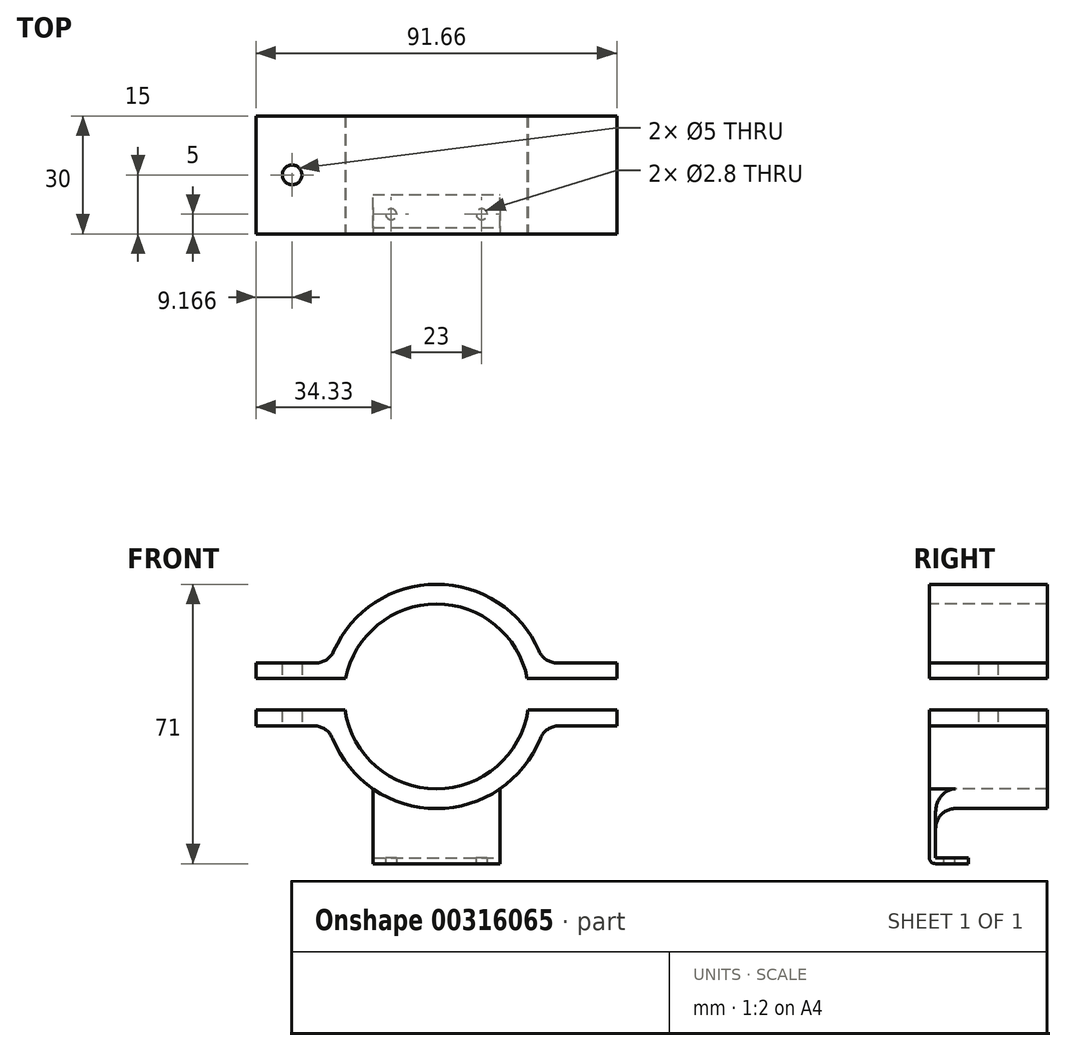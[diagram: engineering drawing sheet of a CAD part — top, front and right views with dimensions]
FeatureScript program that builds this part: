
annotation { "Feature Type Name" : "Feature", "Feature Type Description" : "" }
export const myFeature = defineFeature(function(context is Context, id is Id, definition is map)
    precondition{}
    {
        {
            var Q0;
            Q0=qCreatedBy(makeId("Top.planeOp"),FACE);
            var sketch = newSketch(context, id + "F0", { "sketchPlane" : qUnion([Q0])});
            skCircle(sketch, "E0", {"center": v(-11.5, 0) * mm, "radius": 1.4 * mm});
            skCircle(sketch, "E1", {"center": v(11.5, 0) * mm, "radius": 1.4 * mm});
            skLineSegment(sketch, "E2", {"start": v(-11.5, 0) * mm, "end": v(11.5, 0) * mm, "construction": true});
            skPoint(sketch, "E3", {"position": v(0, 0) * mm});
            skLineSegment(sketch, "E4.bottom", {"start": v(-16.14, -4.96) * mm, "end": v(16.14, -4.96) * mm});
            skLineSegment(sketch, "E4.top", {"start": v(-16.14, 4.96) * mm, "end": v(16.14, 4.96) * mm});
            skLineSegment(sketch, "E4.left", {"start": v(-16.14, -4.96) * mm, "end": v(-16.14, 4.96) * mm});
            skLineSegment(sketch, "E4.right", {"start": v(16.14, -4.96) * mm, "end": v(16.14, 4.96) * mm});
            skLineSegment(sketch, "E5", {"start": v(-11.5, 0) * mm, "end": v(-16.14, 0) * mm, "construction": true});
            skLineSegment(sketch, "E6", {"start": v(11.5, 0) * mm, "end": v(16.14, 0) * mm, "construction": true});
            skLineSegment(sketch, "E7", {"start": v(-11.5, 0) * mm, "end": v(-11.5, -4.96) * mm, "construction": true});
            skLineSegment(sketch, "E8", {"start": v(-11.5, 0) * mm, "end": v(-11.5, 4.96) * mm, "construction": true});
            skSolve(sketch);
        }
        {
            var Q0;
            Q0=makeQuery(id+"F0.imprint","IMPRINT",FACE,{"disambiguationData":[TD([[makeQuery(id+"F0.imprint","IMPRINT",EDGE,{"derivedFrom":sQuery(id+"F0.wireOp",EDGE,"E0")}),-1.0]])]});
            extrude(context, id + "F1", {"entities" : qUnion([Q0]), "depth" : 1.5 * mm});
        }
        {
            var Q0;
            Q0=makeQuery(id+"F1.opExtrude","CAP_FACE",FACE,{"disambiguationData":[OSD([sQuery(id+"F0.wireOp",EDGE,"E0"),sQuery(id+"F0.wireOp",EDGE,"E1"),sQuery(id+"F0.wireOp",EDGE,"E4.bottom"),sQuery(id+"F0.wireOp",EDGE,"E4.top"),sQuery(id+"F0.wireOp",EDGE,"E4.left"),sQuery(id+"F0.wireOp",EDGE,"E4.right")])],"isStart":false});
            var sketch = newSketch(context, id + "F2", { "sketchPlane" : qUnion([Q0])});
            skLineSegment(sketch, "E9.bottom", {"start": v(-16.14, -4.96) * mm, "end": v(16.14, -4.96) * mm});
            skLineSegment(sketch, "E9.top", {"start": v(-16.14, -3.36) * mm, "end": v(16.14, -3.36) * mm});
            skLineSegment(sketch, "E9.left", {"start": v(-16.14, -4.96) * mm, "end": v(-16.14, -3.36) * mm});
            skLineSegment(sketch, "E9.right", {"start": v(16.14, -4.96) * mm, "end": v(16.14, -3.36) * mm});
            skSolve(sketch);
        }
        {
            var Q0;
            Q0=qCreatedBy(makeId("Front.planeOp"),FACE);
            var sketch = newSketch(context, id + "F3", { "sketchPlane" : qUnion([Q0])});
            skArc(sketch, "E10", {"start": v(-22.23, 39) * mm, "mid": v(0, 20) * mm, "end": v(22.23, 39) * mm, "construction": true});
            skArc(sketch, "E11.0", {"start": v(-28.28, 39) * mm, "mid": v(0, 14) * mm, "end": v(28.28, 39) * mm});
            skArc(sketch, "E12.0", {"start": v(-23.24, 39) * mm, "mid": v(0, 19) * mm, "end": v(23.24, 39) * mm});
            skLineSegment(sketch, "E13.bottom", {"start": v(-45.83, 47) * mm, "end": v(-22.05, 47) * mm});
            skLineSegment(sketch, "E13.top", {"start": v(-45.83, 39) * mm, "end": v(-22.23, 39) * mm});
            skLineSegment(sketch, "E14.0", {"start": v(-45.83, 51) * mm, "end": v(-20.83, 51) * mm});
            skLineSegment(sketch, "E14.1", {"start": v(-45.83, 51) * mm, "end": v(-45.83, 47) * mm});
            skLineSegment(sketch, "E14.2", {"start": v(-45.83, 35) * mm, "end": v(-21.21, 35) * mm});
            skLineSegment(sketch, "E14.3", {"start": v(45.83, 51) * mm, "end": v(45.83, 47) * mm});
            skLineSegment(sketch, "E15.trimOffspring", {"start": v(45.83, 39) * mm, "end": v(45.83, 35) * mm});
            skLineSegment(sketch, "E16.trimOffspring", {"start": v(-45.83, 39) * mm, "end": v(-45.83, 35) * mm});
            skArc(sketch, "E17.trimOffspring", {"start": v(22.05, 47) * mm, "mid": v(0, 65) * mm, "end": v(-22.05, 47) * mm, "construction": true});
            skArc(sketch, "E18.trimOffspring", {"start": v(23.07, 47) * mm, "mid": v(0, 66) * mm, "end": v(-23.07, 47) * mm});
            skArc(sketch, "E19.trimOffspring", {"start": v(28.14, 47) * mm, "mid": v(0, 71) * mm, "end": v(-28.14, 47) * mm});
            skLineSegment(sketch, "E20.trimOffspring", {"start": v(22.05, 47) * mm, "end": v(45.83, 47) * mm});
            skLineSegment(sketch, "E21.trimOffspring", {"start": v(20.83, 51) * mm, "end": v(45.83, 51) * mm});
            skLineSegment(sketch, "E22.trimOffspring", {"start": v(22.23, 39) * mm, "end": v(45.83, 39) * mm});
            skLineSegment(sketch, "E23.trimOffspring", {"start": v(21.21, 35) * mm, "end": v(45.83, 35) * mm});
            skSolve(sketch);
        }
        {
            var Q0;
            Q0 = qSketchRegion(id + "F3", true);
            extrude(context, id + "F4", {"entities" : qUnion([Q0]), "operationType" : NewBodyOperationType.ADD, "oppositeDirection" : true, "depth" : 25 * mm, "hasSecondDirection" : true, "secondDirectionOppositeDirection" : false, "secondDirectionDepth" : 5 * mm});
        }
        {
            var Q0;
            Q0=makeQuery(id+"F1.opExtrude","SWEPT_FACE",FACE,{"disambiguationData":[OSD([sQuery(id+"F0.wireOp",EDGE,"E4.bottom")])]});
            var sketch = newSketch(context, id + "F5", { "sketchPlane" : qUnion([Q0])});
            skLineSegment(sketch, "E24", {"start": v(-16.14, 0) * mm, "end": v(-16.14, 19) * mm});
            skLineSegment(sketch, "E25", {"start": v(-16.14, 19) * mm, "end": v(16.14, 19) * mm});
            skLineSegment(sketch, "E26", {"start": v(16.14, 19) * mm, "end": v(16.14, 1.5) * mm});
            skPoint(sketch, "E27", {"position": v(0, 19) * mm});
            skSolve(sketch);
        }
        {
            var Q0;
            {var subQ2=sQuery(id+"F5.wireOp",EDGE,"E25");Q0=makeQuery(id+"F5.imprint","IMPRINT",FACE,{"disambiguationData":[TD([[makeQuery(id+"F5.imprint","IMPRINT",EDGE,{"derivedFrom":subQ2}),-1.0]])]});}
            extrude(context, id + "F6", {"entities" : qUnion([Q0]), "operationType" : NewBodyOperationType.ADD, "oppositeDirection" : true, "depth" : 1.6 * mm});
        }
        {
            var Q0;
            Q0=makeQuery(id+"F1.opExtrude","CAP_EDGE",EDGE,{"disambiguationData":[OSD([sQuery(id+"F0.wireOp",EDGE,"E4.bottom")])],"isStart":true});
            var Q1;
            Q1=makeQuery(id+"F6.opExtrude","CAP_EDGE",EDGE,{"disambiguationData":[OSD([sQuery(id+"F0.wireOp",EDGE,"E4.bottom")])],"isStart":false});
            fillet(context, id + "F7", {"entities" : qUnion([Q0, Q1]), "radius" : 1.5 * mm, "tangentPropagation" : true, "allowEdgeOverflow" : false});
        }
        {
            var Q0;
            Q0=makeQuery(id+"F4.opExtrude","SWEPT_FACE",FACE,{"disambiguationData":[OSD([sQuery(id+"F3.wireOp",EDGE,"E14.2")])]});
            var sketch = newSketch(context, id + "F8", { "sketchPlane" : qUnion([Q0])});
            skCircle(sketch, "E28", {"center": v(-36.66, -10) * mm, "radius": 2.5 * mm});
            skPoint(sketch, "E28.centerSnap0", {"position": v(-45.83, -10) * mm});
            skPoint(sketch, "E28.centerSnap1", {"position": v(-36.66, -25) * mm});
            skSolve(sketch);
        }
        {
            var Q0;
            Q0=makeQuery(id+"F8.imprint","IMPRINT",FACE,{"disambiguationData":[TD([[makeQuery(id+"F8.imprint","IMPRINT",EDGE,{"derivedFrom":sQuery(id+"F8.wireOp",EDGE,"E28")}),1.0]])]});
            extrude(context, id + "F9", {"entities" : qUnion([Q0]), "operationType" : NewBodyOperationType.REMOVE, "oppositeDirection" : true, "depth" : 25 * mm});
        }
        {
            var Q0;
            Q0=makeQuery(id+"F6.boolean.opBoolean","INTERSECT",EDGE,{"derivedFrom":[makeQuery(id+"F4.opExtrude","SWEPT_FACE",FACE,{"disambiguationData":[OSD([sQuery(id+"F3.wireOp",EDGE,"E11.0")])]}),makeQuery(id+"F6.opExtrude","CAP_FACE",FACE,{"disambiguationData":[OSD([sQuery(id+"F0.wireOp",EDGE,"E4.bottom"),sQuery(id+"F5.wireOp",EDGE,"E24"),sQuery(id+"F5.wireOp",EDGE,"E25"),sQuery(id+"F5.wireOp",EDGE,"E26")])],"isStart":false})]});
            fillet(context, id + "F10", {"entities" : qUnion([Q0]), "radius" : 5 * mm, "tangentPropagation" : true, "allowEdgeOverflow" : false});
        }
        {
            var Q0;
            Q0=makeQuery(id+"F4.opExtrude","SWEPT_EDGE",EDGE,{"disambiguationData":[OSD([sQuery(id+"F3.wireOp",EDGE,"E11.0"),sQuery(id+"F3.wireOp",EDGE,"E23.trimOffspring")])]});
            var Q1;
            Q1=makeQuery(id+"F4.opExtrude","SWEPT_EDGE",EDGE,{"disambiguationData":[OSD([sQuery(id+"F3.wireOp",EDGE,"E11.0"),sQuery(id+"F3.wireOp",EDGE,"E14.2")])]});
            var Q2;
            Q2=makeQuery(id+"F4.opExtrude","SWEPT_EDGE",EDGE,{"disambiguationData":[OSD([sQuery(id+"F3.wireOp",EDGE,"E19.trimOffspring"),sQuery(id+"F3.wireOp",EDGE,"E21.trimOffspring")])]});
            var Q3;
            Q3=makeQuery(id+"F4.opExtrude","SWEPT_EDGE",EDGE,{"disambiguationData":[OSD([sQuery(id+"F3.wireOp",EDGE,"E14.0"),sQuery(id+"F3.wireOp",EDGE,"E19.trimOffspring")])]});
            fillet(context, id + "F11", {"entities" : qUnion([Q0, Q1, Q2, Q3]), "radius" : 5 * mm, "tangentPropagation" : true, "allowEdgeOverflow" : false});
        }
    });
